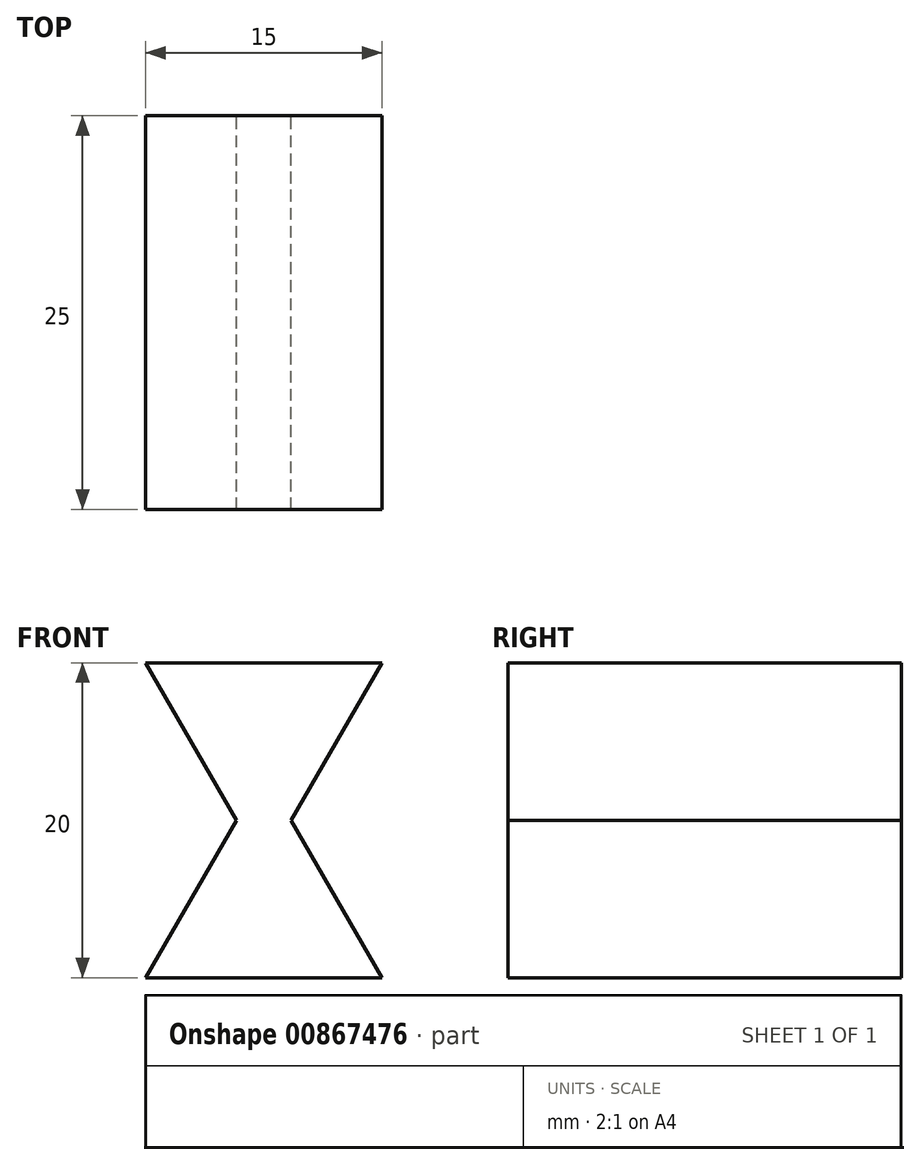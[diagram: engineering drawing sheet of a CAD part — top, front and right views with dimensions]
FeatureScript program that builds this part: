
annotation { "Feature Type Name" : "Feature", "Feature Type Description" : "" }
export const myFeature = defineFeature(function(context is Context, id is Id, definition is map)
    precondition{}
    {
        {
            var Q0;
            Q0=qCreatedBy(makeId("Front.planeOp"),FACE);
            var sketch = newSketch(context, id + "F0", { "sketchPlane" : qUnion([Q0])});
            skLineSegment(sketch, "E0", {"start": v(0, 0) * mm, "end": v(15, 0) * mm});
            skLineSegment(sketch, "E1", {"start": v(0, 20) * mm, "end": v(15, 20) * mm});
            skLineSegment(sketch, "E2", {"start": v(0, 20) * mm, "end": v(5.77, 10) * mm});
            skLineSegment(sketch, "E3", {"start": v(5.77, 10) * mm, "end": v(0, 0) * mm});
            skLineSegment(sketch, "E4", {"start": v(15, 20) * mm, "end": v(9.23, 10) * mm});
            skLineSegment(sketch, "E5", {"start": v(9.23, 10) * mm, "end": v(15, 0) * mm});
            skPoint(sketch, "E6", {"position": v(7.5, 21) * mm});
            skPoint(sketch, "E6.positionSnap0", {"position": v(7.5, 20) * mm});
            skPoint(sketch, "E7", {"position": v(7.5, -1) * mm});
            skPoint(sketch, "E7.positionSnap0", {"position": v(7.5, 0) * mm});
            skPoint(sketch, "E8", {"position": v(1.44, 4.5) * mm});
            skPoint(sketch, "E9", {"position": v(13.56, 4.5) * mm});
            skPoint(sketch, "E10", {"position": v(13.66, 15.67) * mm});
            skPoint(sketch, "E11", {"position": v(0.66, 16.85) * mm});
            skLineSegment(sketch, "E12", {"start": v(10.38, 10) * mm, "end": v(10.04, 10.6) * mm});
            skPoint(sketch, "E13", {"position": v(-1.73, 21) * mm});
            skPoint(sketch, "E14", {"position": v(16.73, 21) * mm});
            skPoint(sketch, "E15", {"position": v(4.62, 10) * mm});
            skPoint(sketch, "E16", {"position": v(10.38, 10) * mm});
            skPoint(sketch, "E17", {"position": v(-1.73, -1) * mm});
            skPoint(sketch, "E18", {"position": v(16.73, -1) * mm});
            skSolve(sketch);
        }
        {
            var Q0;
            Q0=qSketchRegion(id+"F0",true);
            extrude(context, id + "F1", {"entities" : qUnion([Q0]), "depth" : 25 * mm, "offsetDistance" : 25 * mm});
        }
    });
